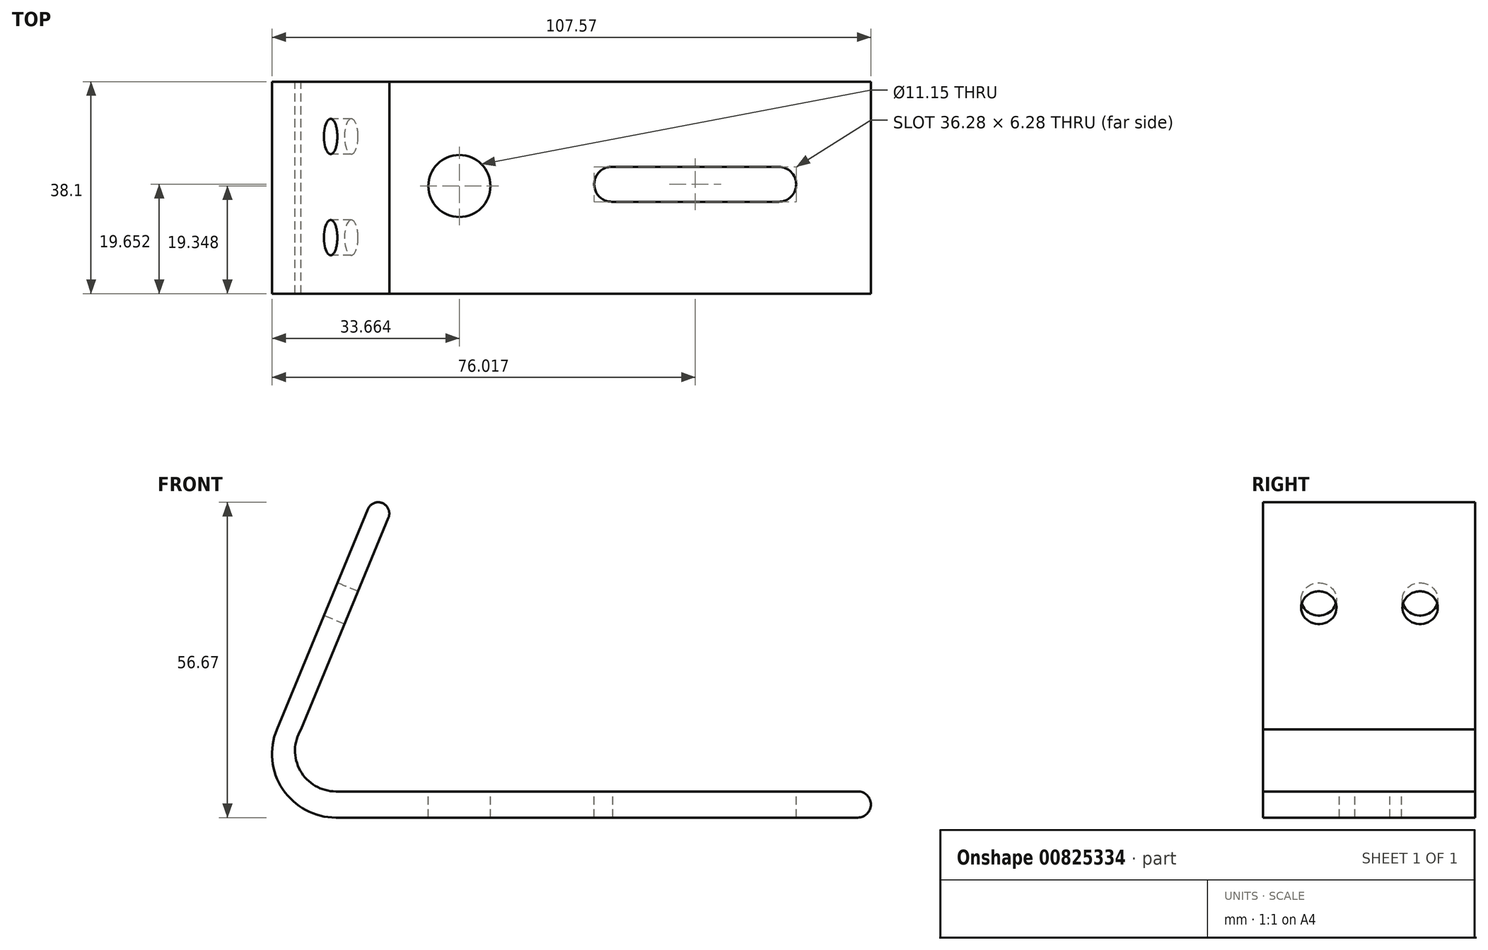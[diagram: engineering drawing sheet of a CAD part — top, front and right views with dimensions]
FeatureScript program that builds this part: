
annotation { "Feature Type Name" : "Feature", "Feature Type Description" : "" }
export const myFeature = defineFeature(function(context is Context, id is Id, definition is map)
    precondition{}
    {
        {
            var Q0;
            Q0=qCreatedBy(makeId("Front.planeOp"),FACE);
            var sketch = newSketch(context, id + "F0", { "sketchPlane" : qUnion([Q0])});
            skLineSegment(sketch, "E0", {"start": v(60.85, 0) * mm, "end": v(-32.9, 0) * mm});
            skLineSegment(sketch, "E1", {"start": v(60.85, 4.7) * mm, "end": v(-32.9, 4.7) * mm});
            skArc(sketch, "E2", {"start": v(-39.16, 15.85) * mm, "mid": v(-39.3, 8.44) * mm, "end": v(-32.9, 4.7) * mm});
            skArc(sketch, "E3", {"start": v(-43.5, 15.85) * mm, "mid": v(-42.43, 5.1) * mm, "end": v(-32.9, 0) * mm});
            skLineSegment(sketch, "E4", {"start": v(-43.5, 15.85) * mm, "end": v(-27.16, 55.41) * mm});
            skLineSegment(sketch, "E5", {"start": v(-39.16, 15.85) * mm, "end": v(-23.45, 53.9) * mm});
            skArc(sketch, "E6", {"start": v(-23.45, 53.9) * mm, "mid": v(-24.55, 56.52) * mm, "end": v(-27.16, 55.41) * mm});
            skArc(sketch, "E7", {"start": v(60.85, 0) * mm, "mid": v(63.2, 2.35) * mm, "end": v(60.85, 4.7) * mm});
            skSolve(sketch);
        }
        {
            var Q0;
            Q0=makeQuery(id+"F0.imprint","IMPRINT",FACE,{"disambiguationData":[TD([[makeQuery(id+"F0.imprint","IMPRINT",EDGE,{"derivedFrom":sQuery(id+"F0.wireOp",EDGE,"E0")}),-1.0]])]});
            extrude(context, id + "F1", {"entities" : qUnion([Q0]), "depth" : 38.1 * mm, "offsetDistance" : 25.4 * mm});
        }
        {
            var Q0;
            Q0=makeQuery(id+"F1.opExtrude","SWEPT_FACE",FACE,{"disambiguationData":[OSD([sQuery(id+"F0.wireOp",EDGE,"E1")])]});
            var sketch = newSketch(context, id + "F2", { "sketchPlane" : qUnion([Q0])});
            skCircle(sketch, "E8", {"center": v(-10.7, -18.75) * mm, "radius": 5.58 * mm});
            skLineSegment(sketch, "E9", {"start": v(16.85, -15.3) * mm, "end": v(46.64, -15.3) * mm});
            skLineSegment(sketch, "E10", {"start": v(46.64, -21.59) * mm, "end": v(16.65, -21.59) * mm});
            skArc(sketch, "E11", {"start": v(46.64, -21.59) * mm, "mid": v(49.79, -18.45) * mm, "end": v(46.64, -15.3) * mm});
            skArc(sketch, "E12", {"start": v(16.85, -15.3) * mm, "mid": v(13.5, -18.34) * mm, "end": v(16.65, -21.59) * mm});
            skSolve(sketch);
        }
        {
            var Q0;
            Q0=makeQuery(id+"F2.imprint","IMPRINT",FACE,{"disambiguationData":[TD([[makeQuery(id+"F2.imprint","IMPRINT",EDGE,{"derivedFrom":sQuery(id+"F2.wireOp",EDGE,"E8")}),1.0]])]});
            var Q1;
            Q1=makeQuery(id+"F2.imprint","IMPRINT",FACE,{"disambiguationData":[TD([[makeQuery(id+"F2.imprint","IMPRINT",EDGE,{"derivedFrom":sQuery(id+"F2.wireOp",EDGE,"E9")}),-1.0]])]});
            extrude(context, id + "F3", {"entities" : qUnion([Q0, Q1]), "operationType" : NewBodyOperationType.REMOVE, "oppositeDirection" : true, "depth" : 25.4 * mm, "offsetDistance" : 25.4 * mm});
        }
        {
            var Q0;
            Q0=makeQuery(id+"F1.opExtrude","SWEPT_FACE",FACE,{"disambiguationData":[OSD([sQuery(id+"F0.wireOp",EDGE,"E4")])]});
            var sketch = newSketch(context, id + "F4", { "sketchPlane" : qUnion([Q0])});
            skCircle(sketch, "E13", {"center": v(9.85, 23.37) * mm, "radius": 3.18 * mm});
            skCircle(sketch, "E14", {"center": v(28.04, 23.37) * mm, "radius": 3.18 * mm});
            skSolve(sketch);
        }
        {
            var Q0;
            Q0 = qSketchRegion(id + "F4", true);
            extrude(context, id + "F5", {"entities" : qUnion([Q0]), "operationType" : NewBodyOperationType.REMOVE, "oppositeDirection" : true, "depth" : 25.4 * mm, "offsetDistance" : 25.4 * mm});
        }
    });
